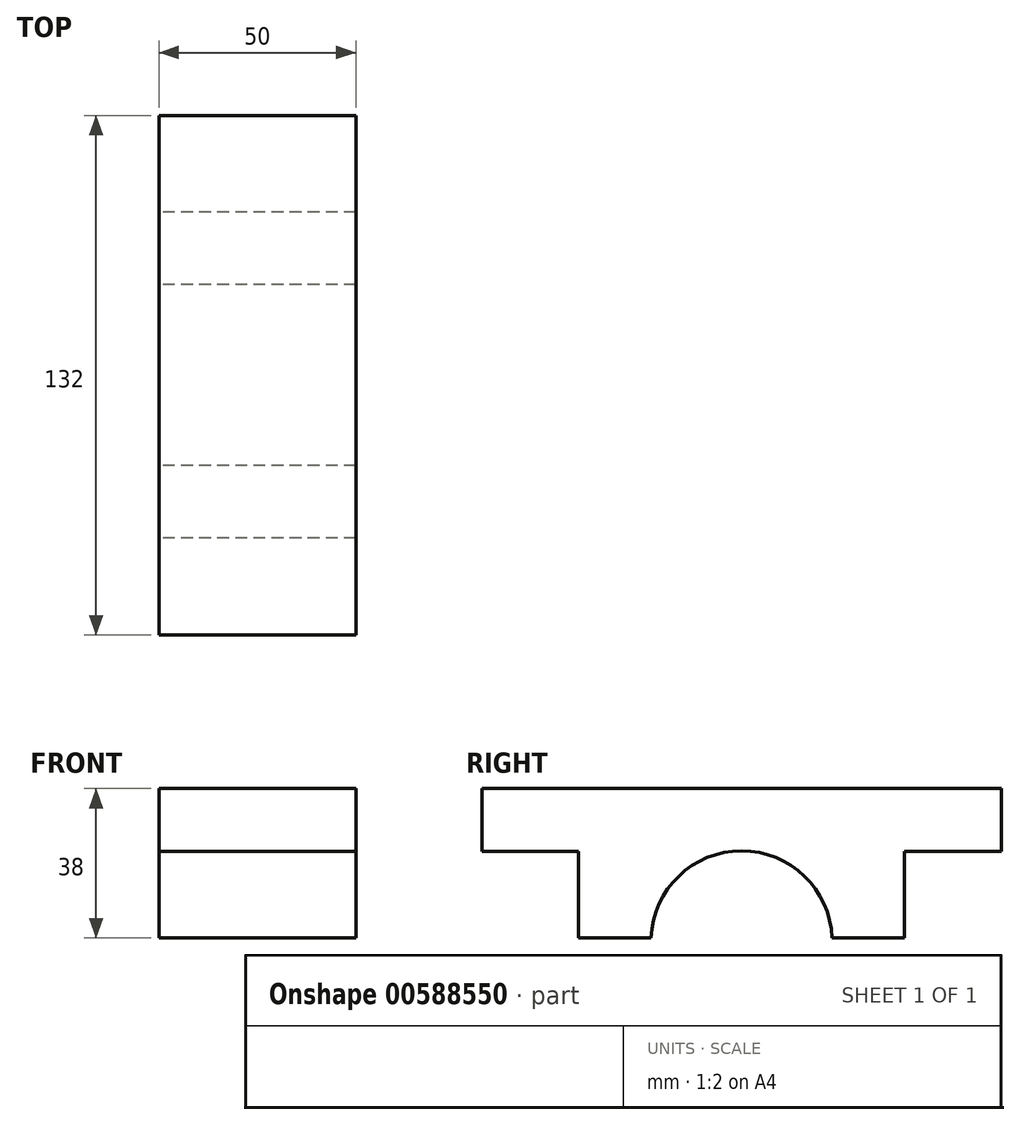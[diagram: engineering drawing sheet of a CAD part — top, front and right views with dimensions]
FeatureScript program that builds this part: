
annotation { "Feature Type Name" : "Feature", "Feature Type Description" : "" }
export const myFeature = defineFeature(function(context is Context, id is Id, definition is map)
    precondition{}
    {
        {
            var Q0;
            Q0=qCreatedBy(makeId("Right.planeOp"),FACE);
            var sketch = newSketch(context, id + "F0", { "sketchPlane" : qUnion([Q0])});
            skLineSegment(sketch, "E0", {"start": v(-68.63, 0) * mm, "end": v(-68.63, 16) * mm});
            skLineSegment(sketch, "E1", {"start": v(-68.63, 16) * mm, "end": v(63.37, 16) * mm});
            skLineSegment(sketch, "E2", {"start": v(63.37, 16) * mm, "end": v(63.37, 0) * mm});
            skLineSegment(sketch, "E3", {"start": v(63.37, 0) * mm, "end": v(38.77, 0) * mm});
            skLineSegment(sketch, "E4", {"start": v(38.77, 0) * mm, "end": v(38.77, -22) * mm});
            skLineSegment(sketch, "E5", {"start": v(38.77, -22) * mm, "end": v(20.37, -22) * mm});
            skLineSegment(sketch, "E6", {"start": v(-68.63, 0) * mm, "end": v(-44.03, 0) * mm});
            skLineSegment(sketch, "E7", {"start": v(-44.03, 0) * mm, "end": v(-44.03, -22) * mm});
            skLineSegment(sketch, "E8", {"start": v(-44.03, -22) * mm, "end": v(-25.63, -22) * mm});
            skArc(sketch, "E9", {"start": v(20.37, -22) * mm, "mid": v(-2.63, 0.15) * mm, "end": v(-25.63, -22) * mm});
            skSolve(sketch);
        }
        {
            var Q0;
            Q0=makeQuery(id+"F0.imprint","IMPRINT",FACE,{"disambiguationData":[TD([[makeQuery(id+"F0.imprint","IMPRINT",EDGE,{"derivedFrom":sQuery(id+"F0.wireOp",EDGE,"E0")}),-1.0]])]});
            extrude(context, id + "F1", {"entities" : qUnion([Q0]), "endBound" : BoundingType.SYMMETRIC, "depth" : 50 * mm, "offsetDistance" : 25 * mm});
        }
    });
